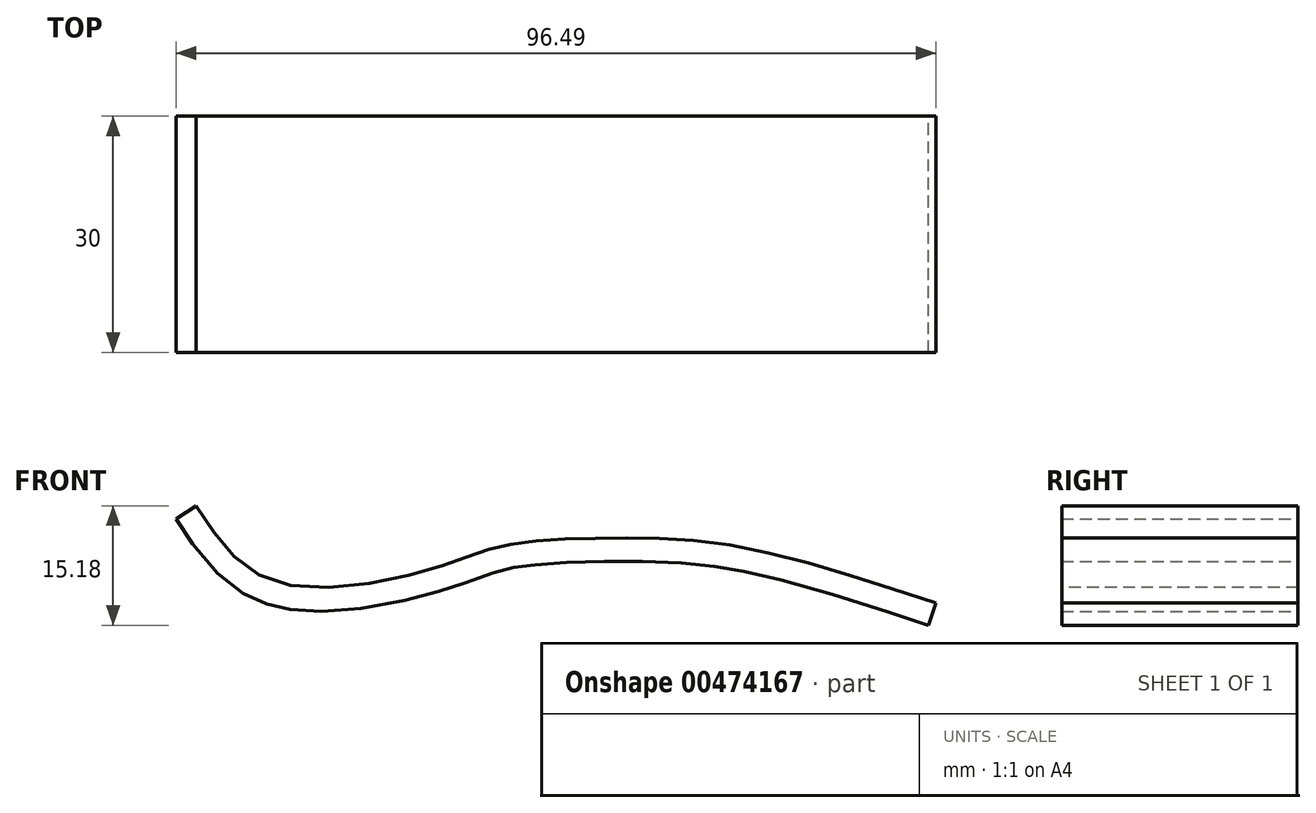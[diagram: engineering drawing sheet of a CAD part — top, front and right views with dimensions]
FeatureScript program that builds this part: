
annotation { "Feature Type Name" : "Feature", "Feature Type Description" : "" }
export const myFeature = defineFeature(function(context is Context, id is Id, definition is map)
    precondition{}
    {
        {
            var Q0;
            Q0=qCreatedBy(makeId("Front.planeOp"),FACE);
            var sketch = newSketch(context, id + "F0", { "sketchPlane" : qUnion([Q0])});
            skFitSpline(sketch, "E0", {"points": [v(0, 0) * mm, v(10.28, -9.7) * mm, v(31.13, -7.64) * mm, v(39.35, -5) * mm, v(51.1, -4.11) * mm, v(67.84, -5) * mm, v(93.98, -12.34) * mm], "startDerivative": vector(51.29, -78.75) * mm, "endDerivative": vector(126.38, -41.76) * mm});
            skFitSpline(sketch, "E1.0", {"points": [v(-2.51, -1.64) * mm, v(-1.98, -2.46) * mm, v(-0.88, -4.14) * mm, v(0.97, -6.68) * mm, v(2.82, -8.69) * mm, v(4.56, -10.14) * mm, v(6, -11.1) * mm, v(7.34, -11.8) * mm, v(8.49, -12.26) * mm, v(9.38, -12.57) * mm, v(10.3, -12.81) * mm, v(11.56, -13.08) * mm, v(13.15, -13.29) * mm, v(15.11, -13.4) * mm, v(17.75, -13.36) * mm, v(21.08, -13.04) * mm, v(24.98, -12.37) * mm, v(28, -11.65) * mm, v(30.22, -11.05) * mm, v(31.75, -10.6) * mm, v(33.12, -10.15) * mm, v(34.75, -9.59) * mm, v(36.48, -8.96) * mm, v(37.93, -8.46) * mm, v(39.05, -8.14) * mm, v(39.77, -7.97) * mm, v(40.38, -7.85) * mm, v(41.02, -7.73) * mm, v(41.89, -7.6) * mm, v(43, -7.48) * mm, v(44.6, -7.35) * mm, v(46.72, -7.23) * mm, v(49.46, -7.14) * mm, v(52.3, -7.09) * mm, v(55.14, -7.05) * mm, v(58.02, -7.08) * mm, v(60.96, -7.2) * mm, v(63.49, -7.42) * mm, v(65.57, -7.68) * mm, v(67.16, -7.91) * mm, v(68.8, -8.2) * mm, v(71.05, -8.65) * mm, v(73.96, -9.34) * mm, v(78.81, -10.64) * mm, v(85.16, -12.58) * mm, v(90.4, -14.31) * mm, v(93.04, -15.18) * mm]});
            skLineSegment(sketch, "E2", {"start": v(0, 0) * mm, "end": v(-2.51, -1.64) * mm});
            skLineSegment(sketch, "E3", {"start": v(93.98, -12.34) * mm, "end": v(93.04, -15.18) * mm});
            skSolve(sketch);
        }
        {
            var Q0;
            Q0 = qSketchRegion(id + "F0", true);
            extrude(context, id + "F1", {"entities" : qUnion([Q0]), "depth" : 30 * mm});
        }
    });
